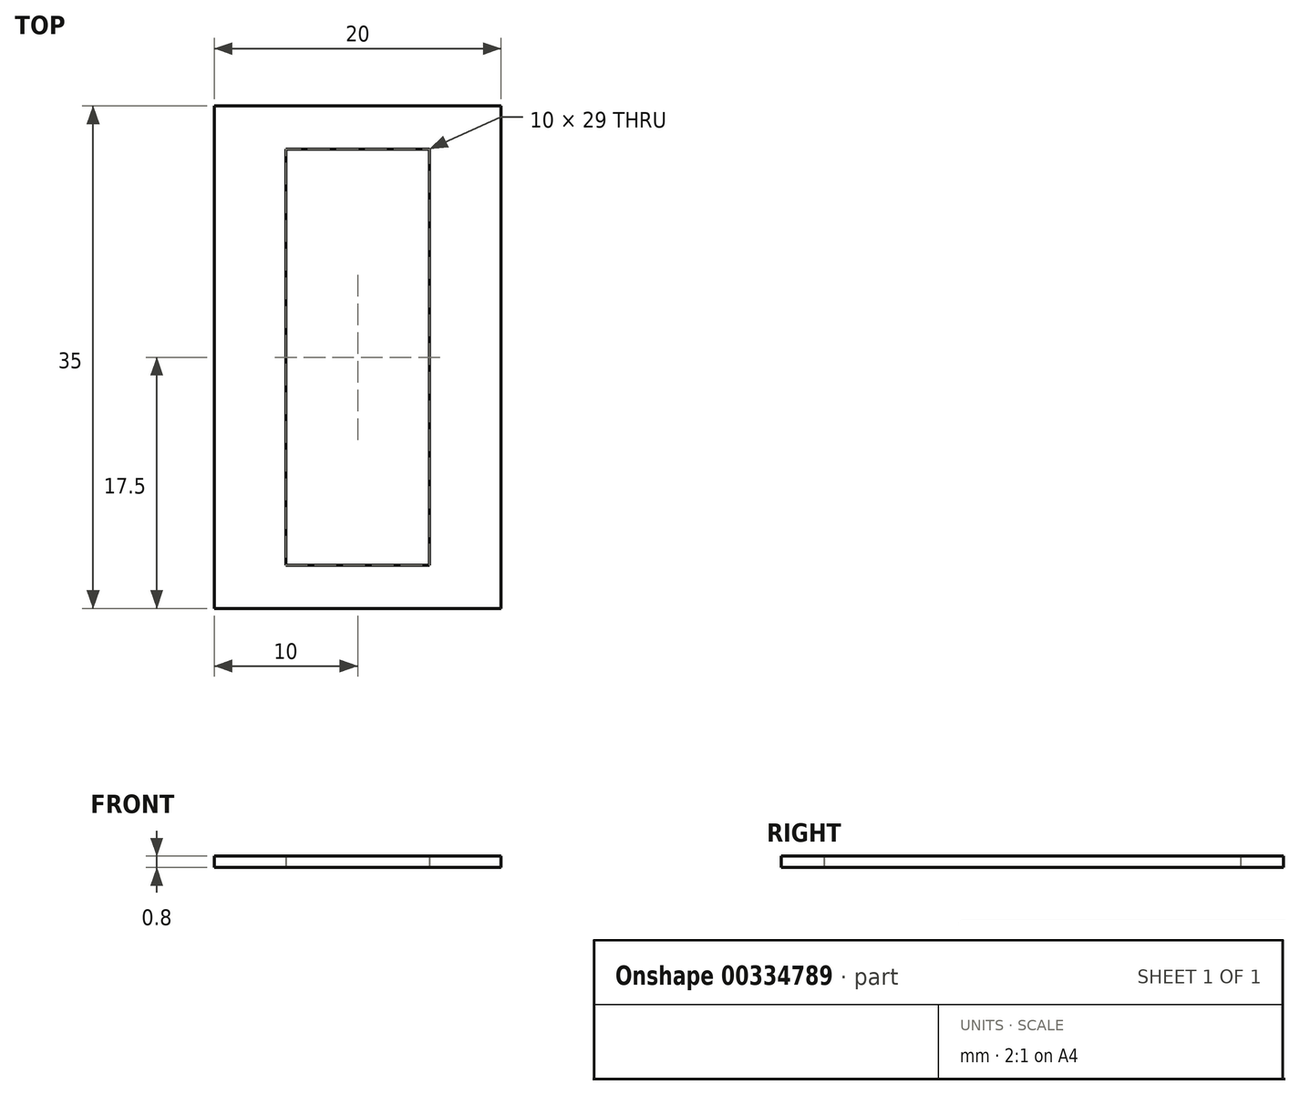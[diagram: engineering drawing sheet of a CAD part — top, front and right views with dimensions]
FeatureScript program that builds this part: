
annotation { "Feature Type Name" : "Feature", "Feature Type Description" : "" }
export const myFeature = defineFeature(function(context is Context, id is Id, definition is map)
    precondition{}
    {
        {
            var Q0;
            Q0=qCreatedBy(makeId("Top.planeOp"),FACE);
            var sketch = newSketch(context, id + "F0", { "sketchPlane" : qUnion([Q0])});
            skLineSegment(sketch, "E0.bottom", {"start": v(-10, 17.5) * mm, "end": v(10, 17.5) * mm});
            skLineSegment(sketch, "E0.top", {"start": v(-10, -17.5) * mm, "end": v(10, -17.5) * mm});
            skLineSegment(sketch, "E0.left", {"start": v(-10, 17.5) * mm, "end": v(-10, -17.5) * mm});
            skLineSegment(sketch, "E0.right", {"start": v(10, 17.5) * mm, "end": v(10, -17.5) * mm});
            skLineSegment(sketch, "E1.bottom", {"start": v(-5, 14.5) * mm, "end": v(5, 14.5) * mm});
            skLineSegment(sketch, "E1.top", {"start": v(-5, -14.5) * mm, "end": v(5, -14.5) * mm});
            skLineSegment(sketch, "E1.left", {"start": v(-5, 14.5) * mm, "end": v(-5, -14.5) * mm});
            skLineSegment(sketch, "E1.right", {"start": v(5, 14.5) * mm, "end": v(5, -14.5) * mm});
            skSolve(sketch);
        }
        {
            var Q0;
            Q0=makeQuery(id+"F0.imprint","IMPRINT",FACE,{"disambiguationData":[TD([[makeQuery(id+"F0.imprint","IMPRINT",EDGE,{"derivedFrom":sQuery(id+"F0.wireOp",EDGE,"E0.bottom")}),-1.0]])]});
            extrude(context, id + "F1", {"entities" : qUnion([Q0]), "depth" : 0.8 * mm});
        }
    });
